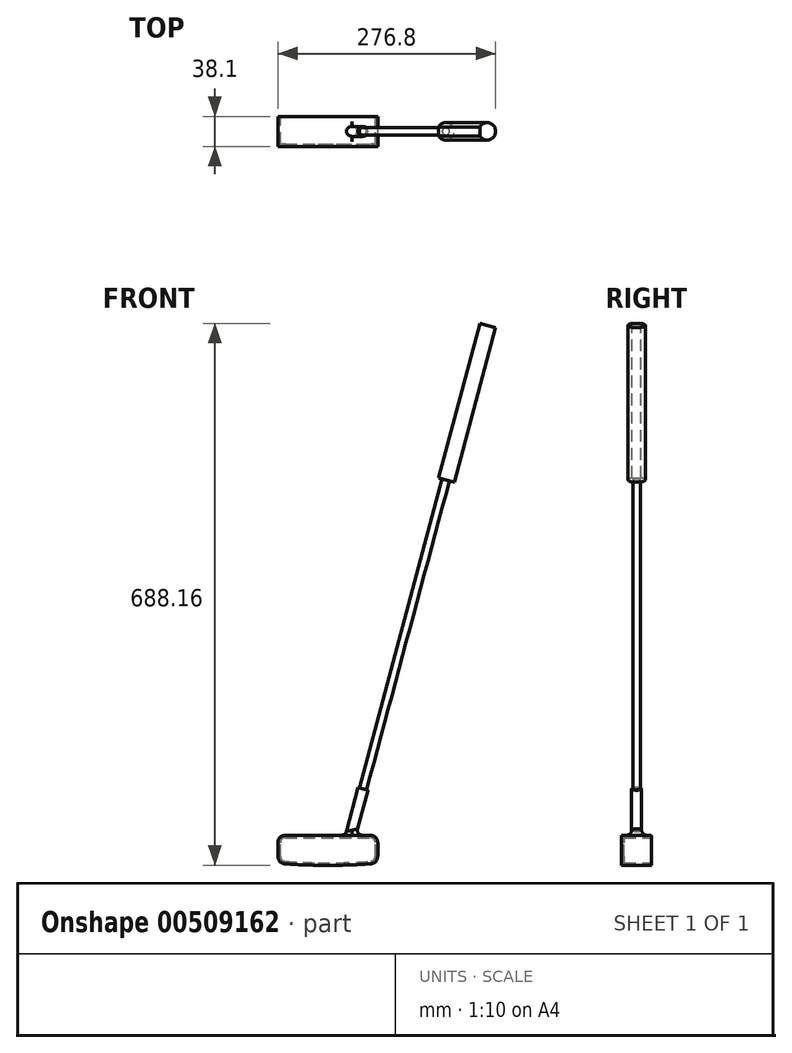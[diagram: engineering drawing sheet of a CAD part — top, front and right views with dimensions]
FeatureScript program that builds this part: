
annotation { "Feature Type Name" : "Feature", "Feature Type Description" : "" }
export const myFeature = defineFeature(function(context is Context, id is Id, definition is map)
    precondition{}
    {
        {
            var Q0;
            Q0=qCreatedBy(makeId("Front.planeOp"),FACE);
            var sketch = newSketch(context, id + "F0", { "sketchPlane" : qUnion([Q0])});
            skLineSegment(sketch, "E0", {"start": v(-12.58, 0) * mm, "end": v(12.58, 0) * mm});
            skArc(sketch, "E1", {"start": v(12.58, 0) * mm, "mid": v(33.69, 0.44) * mm, "end": v(54.77, 1.76) * mm});
            skArc(sketch, "E2", {"start": v(-54.77, 1.76) * mm, "mid": v(-33.69, 0.44) * mm, "end": v(-12.58, 0) * mm});
            skLineSegment(sketch, "E3", {"start": v(63.5, 11.25) * mm, "end": v(63.5, 28.58) * mm});
            skLineSegment(sketch, "E4", {"start": v(-63.5, 11.25) * mm, "end": v(-63.5, 28.58) * mm});
            skLineSegment(sketch, "E5", {"start": v(-53.98, 38.1) * mm, "end": v(53.98, 38.1) * mm});
            skPoint(sketch, "E6.visualSharp", {"position": v(-63.5, 38.1) * mm});
            skArc(sketch, "E6.filletArc", {"start": v(-53.98, 38.1) * mm, "mid": v(-60.71, 35.31) * mm, "end": v(-63.5, 28.58) * mm});
            skPoint(sketch, "E7.visualSharp", {"position": v(63.5, 38.1) * mm});
            skArc(sketch, "E7.filletArc", {"start": v(63.5, 28.58) * mm, "mid": v(60.71, 35.31) * mm, "end": v(53.98, 38.1) * mm});
            skPoint(sketch, "E8.visualSharp", {"position": v(-63.5, 2.56) * mm});
            skArc(sketch, "E8.filletArc", {"start": v(-63.5, 11.25) * mm, "mid": v(-60.98, 4.8) * mm, "end": v(-54.77, 1.76) * mm});
            skPoint(sketch, "E9.visualSharp", {"position": v(63.5, 2.56) * mm});
            skArc(sketch, "E9.filletArc", {"start": v(54.77, 1.76) * mm, "mid": v(60.98, 4.8) * mm, "end": v(63.5, 11.25) * mm});
            skSolve(sketch);
        }
        {
            var Q0;
            Q0=makeQuery(id+"F0.imprint","IMPRINT",FACE,{"disambiguationData":[TD([[makeQuery(id+"F0.imprint","IMPRINT",EDGE,{"derivedFrom":sQuery(id+"F0.wireOp",EDGE,"E0")}),1.0]])]});
            extrude(context, id + "F1", {"entities" : qUnion([Q0]), "endBound" : BoundingType.SYMMETRIC, "depth" : 38.1 * mm});
        }
        {
            var Q0;
            Q0=makeQuery(id+"F1.opExtrude","CAP_FACE",FACE,{"disambiguationData":[OSD([sQuery(id+"F0.wireOp",EDGE,"E0"),sQuery(id+"F0.wireOp",EDGE,"E1"),sQuery(id+"F0.wireOp",EDGE,"E2"),sQuery(id+"F0.wireOp",EDGE,"E3"),sQuery(id+"F0.wireOp",EDGE,"E4"),sQuery(id+"F0.wireOp",EDGE,"E5"),sQuery(id+"F0.wireOp",EDGE,"E6.filletArc"),sQuery(id+"F0.wireOp",EDGE,"E7.filletArc"),sQuery(id+"F0.wireOp",EDGE,"E8.filletArc"),sQuery(id+"F0.wireOp",EDGE,"E9.filletArc")])],"isStart":true});
            shell(context, id + "F2", {"entities" : qUnion([Q0]), "thickness" : 3.17 * mm});
        }
        {
            var Q0;
            Q0=qCreatedBy(makeId("Front.planeOp"),FACE);
            var sketch = newSketch(context, id + "F3", { "sketchPlane" : qUnion([Q0])});
            skLineSegment(sketch, "E10", {"start": v(50.8, 95.25) * mm, "end": v(35.49, 38.1) * mm});
            skLineSegment(sketch, "E11.0", {"start": v(-53.98, 38.1) * mm, "end": v(53.98, 38.1) * mm, "construction": true});
            skLineSegment(sketch, "E12.0", {"start": v(63.5, 11.25) * mm, "end": v(63.5, 28.58) * mm, "construction": true});
            skLineSegment(sketch, "E13", {"start": v(35.49, 38.1) * mm, "end": v(22.34, 38.1) * mm});
            skLineSegment(sketch, "E14", {"start": v(22.34, 38.1) * mm, "end": v(38.53, 98.54) * mm});
            skLineSegment(sketch, "E15", {"start": v(38.53, 98.54) * mm, "end": v(50.8, 95.25) * mm});
            skSolve(sketch);
        }
        {
            var Q0;
            Q0=makeQuery(id+"F3.imprint","IMPRINT",FACE,{"disambiguationData":[TD([[makeQuery(id+"F3.imprint","IMPRINT",EDGE,{"derivedFrom":sQuery(id+"F3.wireOp",EDGE,"E10")}),-1.0]])]});
            extrude(context, id + "F4", {"entities" : qUnion([Q0]), "operationType" : NewBodyOperationType.ADD, "endBound" : BoundingType.SYMMETRIC, "depth" : 12.7 * mm});
        }
        {
            var Q0;
            Q0=makeQuery(id+"F4.opExtrude","CAP_EDGE",EDGE,{"disambiguationData":[OSD([sQuery(id+"F3.wireOp",EDGE,"E10")])],"isStart":true});
            var Q1;
            Q1=makeQuery(id+"F4.opExtrude","CAP_EDGE",EDGE,{"disambiguationData":[OSD([sQuery(id+"F3.wireOp",EDGE,"E14")])],"isStart":true});
            var Q2;
            Q2=makeQuery(id+"F4.opExtrude","CAP_EDGE",EDGE,{"disambiguationData":[OSD([sQuery(id+"F3.wireOp",EDGE,"E10")])],"isStart":false});
            var Q3;
            Q3=makeQuery(id+"F4.opExtrude","CAP_EDGE",EDGE,{"disambiguationData":[OSD([sQuery(id+"F3.wireOp",EDGE,"E14")])],"isStart":false});
            fillet(context, id + "F5", {"entities" : qUnion([Q0, Q1, Q2, Q3]), "radius" : 6.35 * mm, "tangentPropagation" : true, "allowEdgeOverflow" : false});
        }
        {
            var Q0;
            Q0=makeQuery(id+"F5.opFillet","BLEND_EDGE",EDGE,{"blendedFrom":[makeQuery(id+"F4.opExtrude","CAP_EDGE",EDGE,{"disambiguationData":[OSD([sQuery(id+"F3.wireOp",EDGE,"E14")])],"isStart":true}),makeQuery(id+"F1.opExtrude","SWEPT_FACE",FACE,{"disambiguationData":[OSD([sQuery(id+"F0.wireOp",EDGE,"E5")])]})],"blendedInto":[makeQuery(id+"F1.opExtrude","SWEPT_FACE",FACE,{"disambiguationData":[OSD([sQuery(id+"F0.wireOp",EDGE,"E5")])]})]});
            fillet(context, id + "F6", {"entities" : qUnion([Q0]), "radius" : 6.35 * mm, "tangentPropagation" : true, "allowEdgeOverflow" : false});
        }
        {
            var Q0;
            Q0=makeQuery(id+"F4.opExtrude","SWEPT_FACE",FACE,{"disambiguationData":[OSD([sQuery(id+"F3.wireOp",EDGE,"E15")])]});
            var sketch = newSketch(context, id + "F7", { "sketchPlane" : qUnion([Q0])});
            skCircle(sketch, "E16.0", {"center": v(18.07, 0) * mm, "radius": 6.35 * mm});
            skCircle(sketch, "E17", {"center": v(18.07, 0) * mm, "radius": 4.76 * mm});
            skSolve(sketch);
        }
        {
            var Q0;
            Q0=makeQuery(id+"F7.imprint","IMPRINT",FACE,{"disambiguationData":[TD([[makeQuery(id+"F7.imprint","IMPRINT",EDGE,{"derivedFrom":sQuery(id+"F7.wireOp",EDGE,"E17")}),1.0]])]});
            var sketch = newSketch(context, id + "F8", { "sketchPlane" : qUnion([Q0])});
            skSolve(sketch);
        }
        {
            var Q0;
            Q0=makeQuery(id+"F8.imprint","IMPRINT",FACE,{"disambiguationData":[TD([[makeQuery(id+"F8.imprint","IMPRINT",EDGE,{"derivedFrom":makeQuery(id+"F7.imprint","IMPRINT",EDGE,{"derivedFrom":sQuery(id+"F7.wireOp",EDGE,"E17")})}),1.0]])]});
            extrude(context, id + "F9", {"entities" : qUnion([Q0]), "operationType" : NewBodyOperationType.ADD, "depth" : 609.6 * mm});
        }
        {
            var Q0;
            Q0=makeQuery(id+"F9.opExtrude","CAP_FACE",FACE,{"disambiguationData":[OSD([sQuery(id+"F7.wireOp",EDGE,"E17")])],"isStart":false});
            var sketch = newSketch(context, id + "F10", { "sketchPlane" : qUnion([Q0])});
            skLineSegment(sketch, "E18", {"start": v(8.54, -5.72) * mm, "end": v(8.54, 5.72) * mm});
            skArc(sketch, "E19", {"start": v(8.54, -5.72) * mm, "mid": v(29.18, 0) * mm, "end": v(8.54, 5.72) * mm});
            skCircle(sketch, "E20.0", {"center": v(18.07, 0) * mm, "radius": 4.76 * mm});
            skSolve(sketch);
        }
        {
            var Q0;
            Q0=makeQuery(id+"F10.imprint","IMPRINT",FACE,{"disambiguationData":[TD([[makeQuery(id+"F10.imprint","IMPRINT",EDGE,{"derivedFrom":sQuery(id+"F10.wireOp",EDGE,"E18")}),-1.0]])]});
            var Q1;
            Q1=makeQuery(id+"F10.imprint","IMPRINT",FACE,{"disambiguationData":[TD([[makeQuery(id+"F10.imprint","IMPRINT",EDGE,{"derivedFrom":sQuery(id+"F10.wireOp",EDGE,"E20.0")}),1.0]])]});
            extrude(context, id + "F11", {"entities" : qUnion([Q0, Q1]), "operationType" : NewBodyOperationType.ADD, "oppositeDirection" : true, "depth" : 203.2 * mm});
        }
    });
